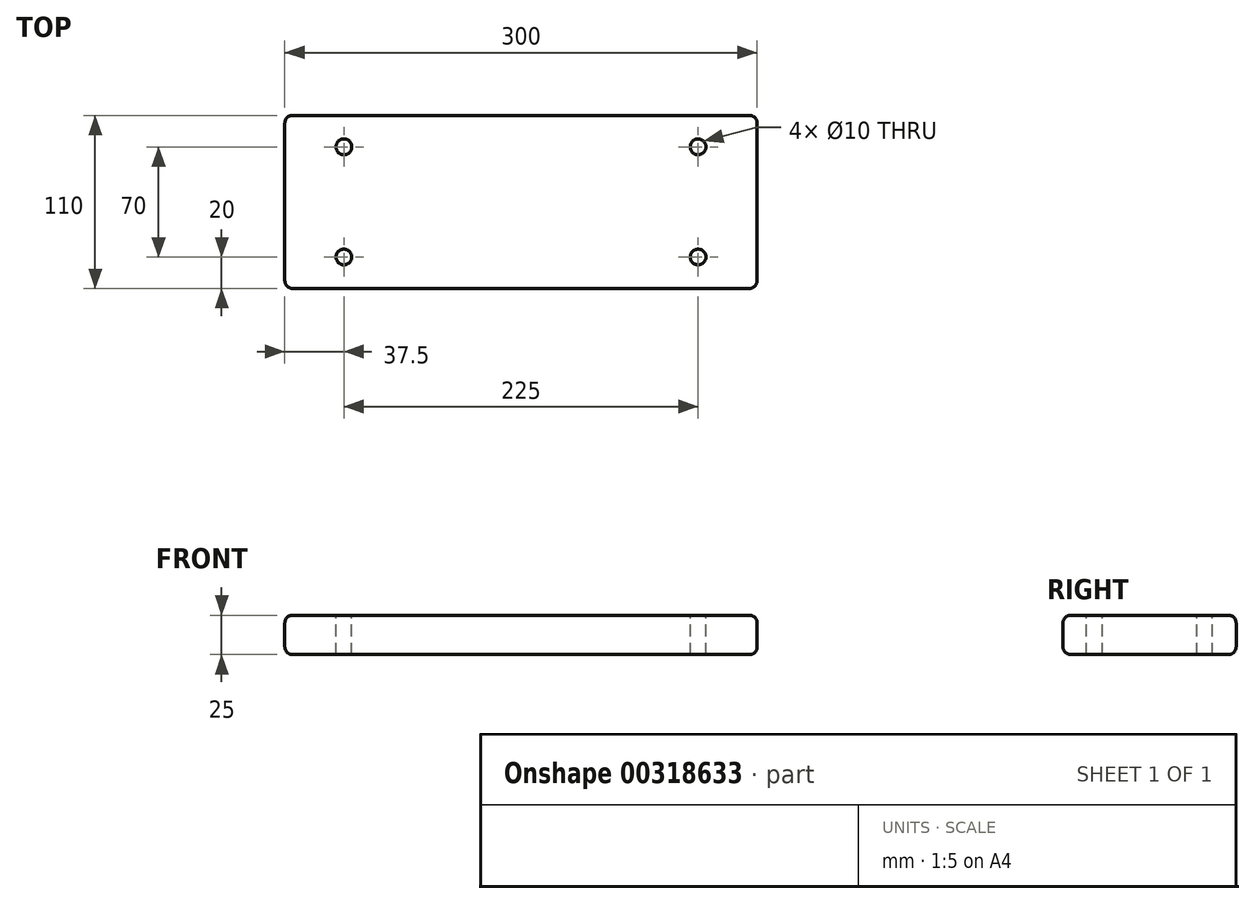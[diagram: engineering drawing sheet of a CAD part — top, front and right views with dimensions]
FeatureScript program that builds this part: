
annotation { "Feature Type Name" : "Feature", "Feature Type Description" : "" }
export const myFeature = defineFeature(function(context is Context, id is Id, definition is map)
    precondition{}
    {
        {
            var Q0;
            Q0=qCreatedBy(makeId("Top.planeOp"),FACE);
            var sketch = newSketch(context, id + "F0", { "sketchPlane" : qUnion([Q0])});
            skLineSegment(sketch, "E0.bottom", {"start": v(150, 55) * mm, "end": v(-150, 55) * mm});
            skLineSegment(sketch, "E0.top", {"start": v(150, -55) * mm, "end": v(-150, -55) * mm});
            skLineSegment(sketch, "E0.left", {"start": v(150, 55) * mm, "end": v(150, -55) * mm});
            skLineSegment(sketch, "E0.right", {"start": v(-150, 55) * mm, "end": v(-150, -55) * mm});
            skPoint(sketch, "E0.middle", {"position": v(0, 0) * mm});
            skSolve(sketch);
        }
        {
            var Q0;
            Q0=makeQuery(id+"F0.imprint","IMPRINT",FACE,{"disambiguationData":[TD([[makeQuery(id+"F0.imprint","IMPRINT",EDGE,{"derivedFrom":sQuery(id+"F0.wireOp",EDGE,"E0.bottom")}),1.0]])]});
            extrude(context, id + "F1", {"entities" : qUnion([Q0]), "depth" : 25 * mm});
        }
        {
            var Q0;
            Q0=makeQuery(id+"F1.opExtrude","CAP_FACE",FACE,{"disambiguationData":[OSD([sQuery(id+"F0.wireOp",EDGE,"E0.bottom"),sQuery(id+"F0.wireOp",EDGE,"E0.top"),sQuery(id+"F0.wireOp",EDGE,"E0.left"),sQuery(id+"F0.wireOp",EDGE,"E0.right")])],"isStart":false});
            var sketch = newSketch(context, id + "F2", { "sketchPlane" : qUnion([Q0])});
            skLineSegment(sketch, "E1.bottom", {"start": v(112.5, 35) * mm, "end": v(-112.5, 35) * mm, "construction": true});
            skLineSegment(sketch, "E1.top", {"start": v(112.5, -35) * mm, "end": v(-112.5, -35) * mm, "construction": true});
            skLineSegment(sketch, "E1.left", {"start": v(112.5, 35) * mm, "end": v(112.5, -35) * mm, "construction": true});
            skLineSegment(sketch, "E1.right", {"start": v(-112.5, 35) * mm, "end": v(-112.5, -35) * mm, "construction": true});
            skPoint(sketch, "E1.middle", {"position": v(0, 0) * mm});
            skCircle(sketch, "E2", {"center": v(-112.5, 35) * mm, "radius": 5 * mm});
            skCircle(sketch, "E3", {"center": v(-112.5, -35) * mm, "radius": 5 * mm});
            skCircle(sketch, "E4", {"center": v(112.5, -35) * mm, "radius": 5 * mm});
            skCircle(sketch, "E5", {"center": v(112.5, 35) * mm, "radius": 5 * mm});
            skSolve(sketch);
        }
        {
            var Q0;
            Q0=makeQuery(id+"F2.imprint","IMPRINT",FACE,{"disambiguationData":[TD([[makeQuery(id+"F2.imprint","IMPRINT",EDGE,{"derivedFrom":sQuery(id+"F2.wireOp",EDGE,"E2")}),1.0]])]});
            var Q1;
            Q1=makeQuery(id+"F2.imprint","IMPRINT",FACE,{"disambiguationData":[TD([[makeQuery(id+"F2.imprint","IMPRINT",EDGE,{"derivedFrom":sQuery(id+"F2.wireOp",EDGE,"E3")}),1.0]])]});
            var Q2;
            Q2=makeQuery(id+"F2.imprint","IMPRINT",FACE,{"disambiguationData":[TD([[makeQuery(id+"F2.imprint","IMPRINT",EDGE,{"derivedFrom":sQuery(id+"F2.wireOp",EDGE,"E4")}),1.0]])]});
            var Q3;
            Q3=makeQuery(id+"F2.imprint","IMPRINT",FACE,{"disambiguationData":[TD([[makeQuery(id+"F2.imprint","IMPRINT",EDGE,{"derivedFrom":sQuery(id+"F2.wireOp",EDGE,"E5")}),1.0]])]});
            extrude(context, id + "F3", {"entities" : qUnion([Q0, Q1, Q2, Q3]), "operationType" : NewBodyOperationType.REMOVE, "endBound" : BoundingType.THROUGH_ALL, "oppositeDirection" : true, "depth" : 25 * mm});
        }
        {
            var Q0;
            Q0=makeQuery(id+"F1.opExtrude","CAP_EDGE",EDGE,{"disambiguationData":[OSD([sQuery(id+"F0.wireOp",EDGE,"E0.bottom")])],"isStart":false});
            var Q1;
            Q1=makeQuery(id+"F1.opExtrude","CAP_EDGE",EDGE,{"disambiguationData":[OSD([sQuery(id+"F0.wireOp",EDGE,"E0.right")])],"isStart":false});
            var Q2;
            Q2=makeQuery(id+"F1.opExtrude","CAP_EDGE",EDGE,{"disambiguationData":[OSD([sQuery(id+"F0.wireOp",EDGE,"E0.top")])],"isStart":false});
            var Q3;
            Q3=makeQuery(id+"F1.opExtrude","CAP_EDGE",EDGE,{"disambiguationData":[OSD([sQuery(id+"F0.wireOp",EDGE,"E0.left")])],"isStart":false});
            var Q4;
            Q4=makeQuery(id+"F1.opExtrude","CAP_EDGE",EDGE,{"disambiguationData":[OSD([sQuery(id+"F0.wireOp",EDGE,"E0.left")])],"isStart":true});
            var Q5;
            Q5=makeQuery(id+"F1.opExtrude","CAP_EDGE",EDGE,{"disambiguationData":[OSD([sQuery(id+"F0.wireOp",EDGE,"E0.bottom")])],"isStart":true});
            var Q6;
            Q6=makeQuery(id+"F1.opExtrude","CAP_EDGE",EDGE,{"disambiguationData":[OSD([sQuery(id+"F0.wireOp",EDGE,"E0.right")])],"isStart":true});
            var Q7;
            Q7=makeQuery(id+"F1.opExtrude","SWEPT_EDGE",EDGE,{"disambiguationData":[OSD([sQuery(id+"F0.wireOp",EDGE,"E0.top"),sQuery(id+"F0.wireOp",EDGE,"E0.right")])]});
            var Q8;
            Q8=makeQuery(id+"F1.opExtrude","SWEPT_EDGE",EDGE,{"disambiguationData":[OSD([sQuery(id+"F0.wireOp",EDGE,"E0.bottom"),sQuery(id+"F0.wireOp",EDGE,"E0.right")])]});
            var Q9;
            Q9=makeQuery(id+"F1.opExtrude","SWEPT_EDGE",EDGE,{"disambiguationData":[OSD([sQuery(id+"F0.wireOp",EDGE,"E0.bottom"),sQuery(id+"F0.wireOp",EDGE,"E0.left")])]});
            var Q10;
            Q10=makeQuery(id+"F1.opExtrude","SWEPT_EDGE",EDGE,{"disambiguationData":[OSD([sQuery(id+"F0.wireOp",EDGE,"E0.top"),sQuery(id+"F0.wireOp",EDGE,"E0.left")])]});
            var Q11;
            Q11=makeQuery(id+"F1.opExtrude","CAP_EDGE",EDGE,{"disambiguationData":[OSD([sQuery(id+"F0.wireOp",EDGE,"E0.top")])],"isStart":true});
            fillet(context, id + "F4", {"entities" : qUnion([Q0, Q1, Q2, Q3, Q4, Q5, Q6, Q7, Q8, Q9, Q10, Q11]), "radius" : 5 * mm, "tangentPropagation" : true, "allowEdgeOverflow" : false});
        }
    });
